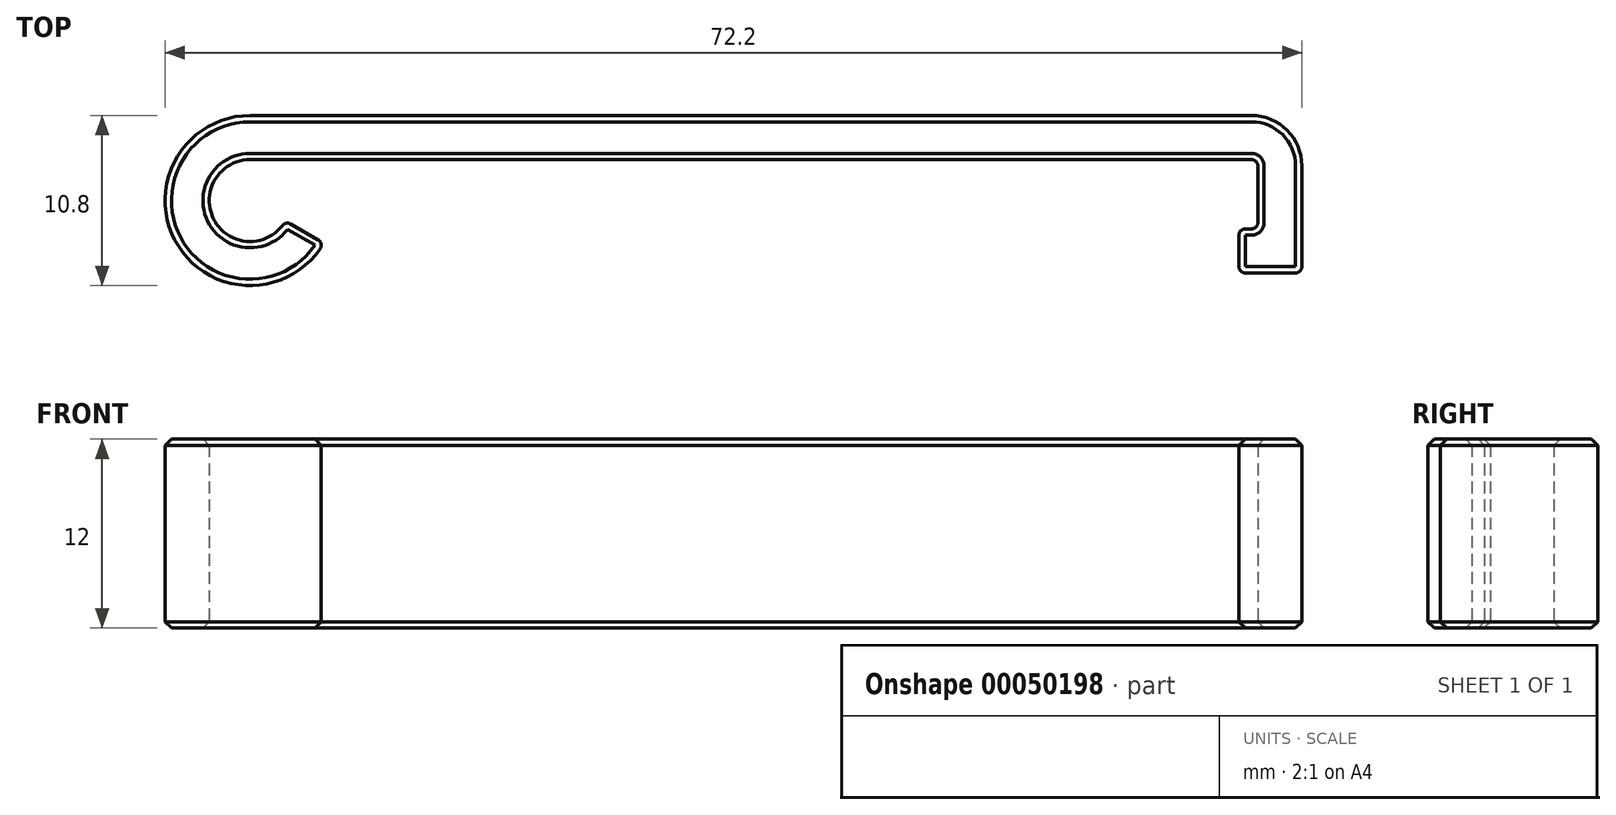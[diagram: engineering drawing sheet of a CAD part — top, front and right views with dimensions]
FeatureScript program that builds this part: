
annotation { "Feature Type Name" : "Feature", "Feature Type Description" : "" }
export const myFeature = defineFeature(function(context is Context, id is Id, definition is map)
    precondition{}
    {
        {
            var Q0;
            Q0=qCreatedBy(makeId("Top.planeOp"),FACE);
            var sketch = newSketch(context, id + "F0", { "sketchPlane" : qUnion([Q0])});
            skLineSegment(sketch, "E0", {"start": v(32, 0) * mm, "end": v(-32, 0) * mm});
            skLineSegment(sketch, "E1", {"start": v(32, 0) * mm, "end": v(32, -4.4) * mm});
            skLineSegment(sketch, "E2", {"start": v(32, -4.4) * mm, "end": v(30.8, -4.4) * mm});
            skLineSegment(sketch, "E3", {"start": v(30.8, -4.4) * mm, "end": v(30.8, -7.2) * mm});
            skLineSegment(sketch, "E4", {"start": v(30.8, -7.2) * mm, "end": v(34.8, -7.2) * mm});
            skLineSegment(sketch, "E5", {"start": v(34.8, -7.2) * mm, "end": v(34.8, 2.8) * mm});
            skLineSegment(sketch, "E6", {"start": v(34.8, 2.8) * mm, "end": v(-32, 2.8) * mm});
            skCircle(sketch, "E7", {"center": v(-32, -2.6) * mm, "radius": 5.4 * mm, "construction": true});
            skCircle(sketch, "E8", {"center": v(-32, -2.6) * mm, "radius": 2.6 * mm, "construction": true});
            skLineSegment(sketch, "E9", {"start": v(-29.75, -3.9) * mm, "end": v(-27.32, -5.3) * mm});
            skLineSegment(sketch, "E10", {"start": v(-29.75, -3.9) * mm, "end": v(-32, -2.6) * mm, "construction": true});
            skArc(sketch, "E11", {"start": v(-32, 0) * mm, "mid": v(-34.25, -3.9) * mm, "end": v(-29.75, -3.9) * mm});
            skArc(sketch, "E12", {"start": v(-32, 2.8) * mm, "mid": v(-36.68, -5.3) * mm, "end": v(-27.32, -5.3) * mm});
            skSolve(sketch);
        }
        {
            var Q0;
            Q0=makeQuery(id+"F0.imprint","IMPRINT",FACE,{"disambiguationData":[TD([[makeQuery(id+"F0.imprint","IMPRINT",EDGE,{"derivedFrom":sQuery(id+"F0.wireOp",EDGE,"E0")}),-1.0]])]});
            extrude(context, id + "F1", {"entities" : qUnion([Q0]), "depth" : 12 * mm});
        }
        {
            var Q0;
            Q0=makeQuery(id+"F1.opExtrude","SWEPT_EDGE",EDGE,{"disambiguationData":[OSD([sQuery(id+"F0.wireOp",EDGE,"E0"),sQuery(id+"F0.wireOp",EDGE,"E1")])]});
            var Q1;
            Q1=makeQuery(id+"F1.opExtrude","SWEPT_EDGE",EDGE,{"disambiguationData":[OSD([sQuery(id+"F0.wireOp",EDGE,"E1"),sQuery(id+"F0.wireOp",EDGE,"E2")])]});
            var Q2;
            Q2=makeQuery(id+"F1.opExtrude","SWEPT_EDGE",EDGE,{"disambiguationData":[OSD([sQuery(id+"F0.wireOp",EDGE,"E3"),sQuery(id+"F0.wireOp",EDGE,"E4")])]});
            var Q3;
            Q3=makeQuery(id+"F1.opExtrude","SWEPT_EDGE",EDGE,{"disambiguationData":[OSD([sQuery(id+"F0.wireOp",EDGE,"E4"),sQuery(id+"F0.wireOp",EDGE,"E5")])]});
            var Q4;
            Q4=makeQuery(id+"F1.opExtrude","SWEPT_EDGE",EDGE,{"disambiguationData":[OSD([sQuery(id+"F0.wireOp",EDGE,"E2"),sQuery(id+"F0.wireOp",EDGE,"E3")])]});
            var Q5;
            Q5=makeQuery(id+"F1.opExtrude","SWEPT_EDGE",EDGE,{"disambiguationData":[OSD([sQuery(id+"F0.wireOp",EDGE,"E9"),sQuery(id+"F0.wireOp",EDGE,"E11")])]});
            var Q6;
            Q6=makeQuery(id+"F1.opExtrude","SWEPT_EDGE",EDGE,{"disambiguationData":[OSD([sQuery(id+"F0.wireOp",EDGE,"E9"),sQuery(id+"F0.wireOp",EDGE,"E12")])]});
            fillet(context, id + "F2", {"entities" : qUnion([Q0, Q1, Q2, Q3, Q4, Q5, Q6]), "radius" : .4 * mm, "tangentPropagation" : true, "allowEdgeOverflow" : false});
        }
        {
            var Q0;
            Q0=makeQuery(id+"F1.opExtrude","SWEPT_EDGE",EDGE,{"disambiguationData":[OSD([sQuery(id+"F0.wireOp",EDGE,"E5"),sQuery(id+"F0.wireOp",EDGE,"E6")])]});
            fillet(context, id + "F3", {"entities" : qUnion([Q0]), "radius" : (2.8 + .4) * mm, "tangentPropagation" : true, "allowEdgeOverflow" : false});
        }
        {
            var Q0;
            Q0=makeQuery(id+"F1.opExtrude","CAP_FACE",FACE,{"disambiguationData":[OSD([sQuery(id+"F0.wireOp",EDGE,"E0"),sQuery(id+"F0.wireOp",EDGE,"E1"),sQuery(id+"F0.wireOp",EDGE,"E2"),sQuery(id+"F0.wireOp",EDGE,"E3"),sQuery(id+"F0.wireOp",EDGE,"E4"),sQuery(id+"F0.wireOp",EDGE,"E5"),sQuery(id+"F0.wireOp",EDGE,"E6"),sQuery(id+"F0.wireOp",EDGE,"E9"),sQuery(id+"F0.wireOp",EDGE,"E11"),sQuery(id+"F0.wireOp",EDGE,"E12")])],"isStart":false});
            var Q1;
            Q1=makeQuery(id+"F1.opExtrude","CAP_FACE",FACE,{"disambiguationData":[OSD([sQuery(id+"F0.wireOp",EDGE,"E0"),sQuery(id+"F0.wireOp",EDGE,"E1"),sQuery(id+"F0.wireOp",EDGE,"E2"),sQuery(id+"F0.wireOp",EDGE,"E3"),sQuery(id+"F0.wireOp",EDGE,"E4"),sQuery(id+"F0.wireOp",EDGE,"E5"),sQuery(id+"F0.wireOp",EDGE,"E6"),sQuery(id+"F0.wireOp",EDGE,"E9"),sQuery(id+"F0.wireOp",EDGE,"E11"),sQuery(id+"F0.wireOp",EDGE,"E12")])],"isStart":true});
            chamfer(context, id + "F4", {"entities" : qUnion([Q0, Q1]), "width" : .4 * mm, "tangentPropagation" : true});
        }
    });
